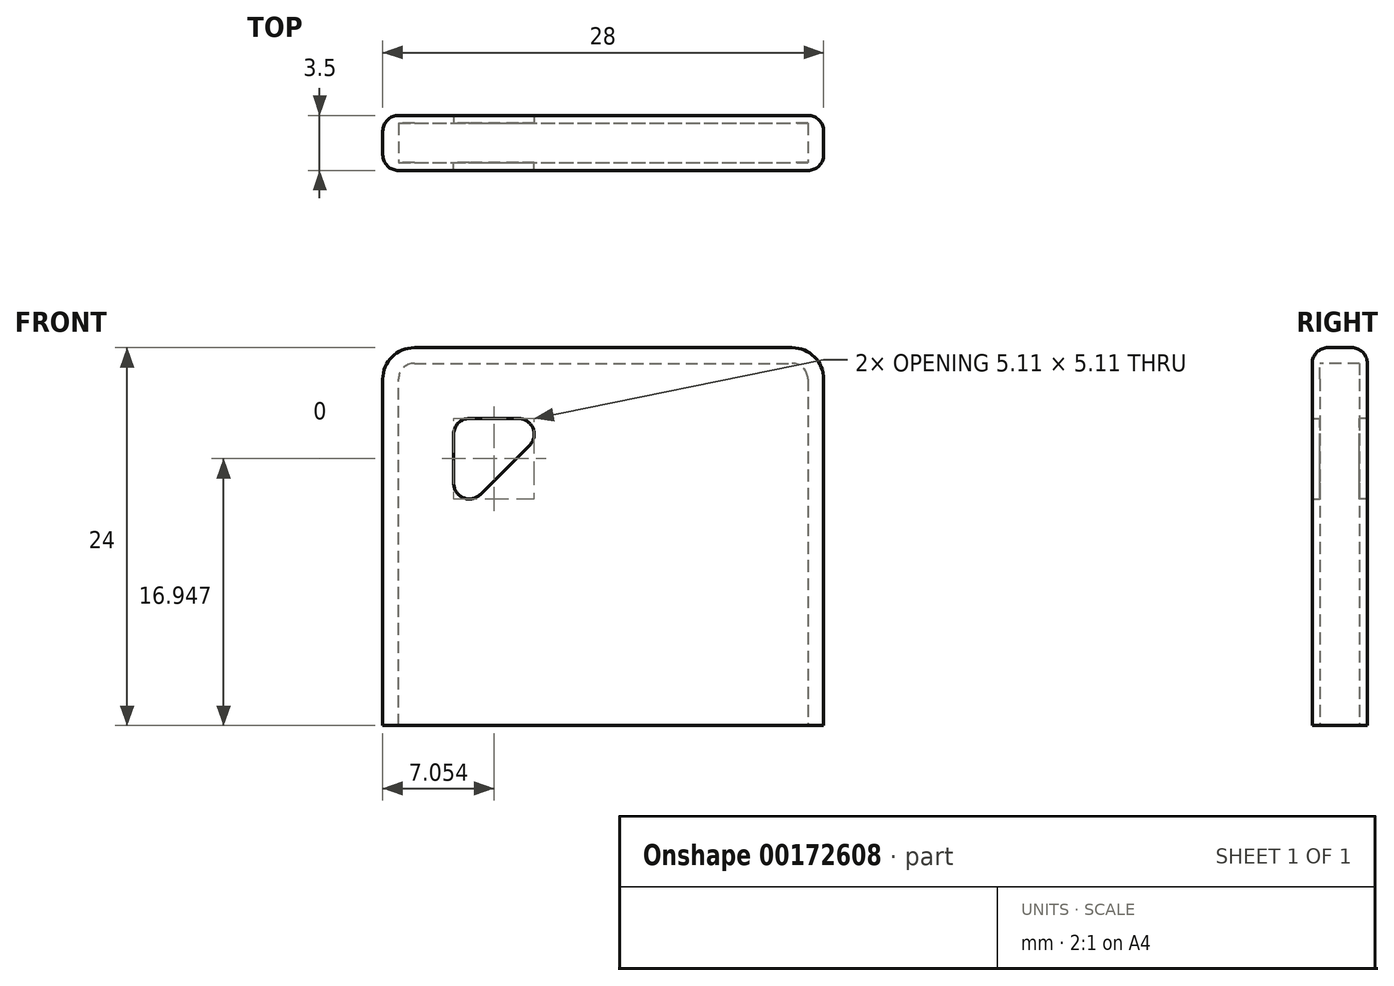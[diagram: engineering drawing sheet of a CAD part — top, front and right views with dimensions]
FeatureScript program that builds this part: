
annotation { "Feature Type Name" : "Feature", "Feature Type Description" : "" }
export const myFeature = defineFeature(function(context is Context, id is Id, definition is map)
    precondition{}
    {
        {
            var Q0;
            Q0=qCreatedBy(makeId("Front.planeOp"),FACE);
            var sketch = newSketch(context, id + "F0", { "sketchPlane" : qUnion([Q0])});
            skLineSegment(sketch, "E0", {"start": v(-50.86, -19) * mm, "end": v(-22.86, -19) * mm});
            skLineSegment(sketch, "E1", {"start": v(-22.86, -19) * mm, "end": v(-22.86, 0) * mm});
            skLineSegment(sketch, "E2", {"start": v(-50.86, -19) * mm, "end": v(-50.86, 0) * mm});
            skLineSegment(sketch, "E3", {"start": v(-45.86, 5) * mm, "end": v(-27.86, 5) * mm});
            skLineSegment(sketch, "E4", {"start": v(-50.86, -19) * mm, "end": v(-50.86, 3) * mm});
            skLineSegment(sketch, "E5", {"start": v(-48.86, 5) * mm, "end": v(-24.86, 5) * mm});
            skLineSegment(sketch, "E6", {"start": v(-22.86, -19) * mm, "end": v(-22.86, 3) * mm});
            skArc(sketch, "E7.filletArc", {"start": v(-22.86, 3) * mm, "mid": v(-23.45, 4.41) * mm, "end": v(-24.86, 5) * mm});
            skArc(sketch, "E8.filletArc", {"start": v(-48.86, 5) * mm, "mid": v(-50.27, 4.41) * mm, "end": v(-50.86, 3) * mm});
            skLineSegment(sketch, "E9", {"start": v(-44.65, -4.32) * mm, "end": v(-41.54, -1.2) * mm});
            skLineSegment(sketch, "E10", {"start": v(-46.36, -3.61) * mm, "end": v(-46.36, -0.5) * mm});
            skLineSegment(sketch, "E11", {"start": v(-42.25, 0.5) * mm, "end": v(-45.36, 0.5) * mm});
            skArc(sketch, "E12.filletArc", {"start": v(-45.36, 0.5) * mm, "mid": v(-46.07, 0.2) * mm, "end": v(-46.36, -0.5) * mm});
            skArc(sketch, "E13.filletArc", {"start": v(-41.54, -1.2) * mm, "mid": v(-41.32, -0.12) * mm, "end": v(-42.25, 0.5) * mm});
            skArc(sketch, "E14.filletArc", {"start": v(-46.36, -3.61) * mm, "mid": v(-45.74, -4.54) * mm, "end": v(-44.65, -4.32) * mm});
            skLineSegment(sketch, "E15", {"start": v(-49.86, -19) * mm, "end": v(-49.86, 3) * mm});
            skLineSegment(sketch, "E16", {"start": v(-48.86, 4) * mm, "end": v(-24.86, 4) * mm});
            skLineSegment(sketch, "E17", {"start": v(-23.86, 3) * mm, "end": v(-23.86, -19) * mm});
            skPoint(sketch, "E18.visualSharp", {"position": v(-49.86, 4) * mm});
            skArc(sketch, "E18.filletArc", {"start": v(-48.86, 4) * mm, "mid": v(-49.57, 3.7) * mm, "end": v(-49.86, 3) * mm});
            skPoint(sketch, "E19.visualSharp", {"position": v(-23.86, 4) * mm});
            skArc(sketch, "E19.filletArc", {"start": v(-23.86, 3) * mm, "mid": v(-24.15, 3.7) * mm, "end": v(-24.86, 4) * mm});
            skSolve(sketch);
        }
        {
            var Q0;
            {var subQ5=sQuery(id+"F0.wireOp",EDGE,"E7.filletArc");Q0=makeQuery(id+"F0.imprint","IMPRINT",FACE,{"disambiguationData":[TD([[makeQuery(id+"F0.imprint","IMPRINT",EDGE,{"derivedFrom":subQ5}),1.0]])]});}
            var Q1;
            Q1=makeQuery(id+"F0.imprint","IMPRINT",FACE,{"disambiguationData":[TD([[makeQuery(id+"F0.imprint","IMPRINT",EDGE,{"derivedFrom":sQuery(id+"F0.wireOp",EDGE,"E9")}),-1.0]])]});
            extrude(context, id + "F1", {"entities" : qUnion([Q0, Q1]), "depth" : 0.5 * mm});
        }
        {
            var Q0;
            {var subQ5=sQuery(id+"F0.wireOp",EDGE,"E7.filletArc");Q0=makeQuery(id+"F0.imprint","IMPRINT",FACE,{"disambiguationData":[TD([[makeQuery(id+"F0.imprint","IMPRINT",EDGE,{"derivedFrom":subQ5}),1.0]])]});}
            extrude(context, id + "F2", {"entities" : qUnion([Q0]), "operationType" : NewBodyOperationType.ADD, "oppositeDirection" : true, "depth" : 1.25 * mm});
        }
        {
            var Q0;
            Q0=makeQuery(id+"F2.opExtrude","CAP_FACE",FACE,{"disambiguationData":[OSD([sQuery(id+"F0.wireOp",EDGE,"E0"),sQuery(id+"F0.wireOp",EDGE,"E4"),sQuery(id+"F0.wireOp",EDGE,"E5"),sQuery(id+"F0.wireOp",EDGE,"E6"),sQuery(id+"F0.wireOp",EDGE,"E7.filletArc"),sQuery(id+"F0.wireOp",EDGE,"E8.filletArc"),sQuery(id+"F0.wireOp",EDGE,"E15"),sQuery(id+"F0.wireOp",EDGE,"E16"),sQuery(id+"F0.wireOp",EDGE,"E17"),sQuery(id+"F0.wireOp",EDGE,"E18.filletArc"),sQuery(id+"F0.wireOp",EDGE,"E19.filletArc")])],"isStart":false});
            cPlane(context, id + "F3", {"entities" : qUnion([Q0]), "cplaneType" : CPlaneType.OFFSET, "offset" : 0 * mm, "width" : 150 * mm, "height" : 150 * mm});
        }
        {
            var Q0;
            Q0=makeQuery(id+"F1.opExtrude","SWEPT_BODY",BODY,{"disambiguationData":[OSD([sQuery(id+"F0.wireOp",EDGE,"E0"),sQuery(id+"F0.wireOp",EDGE,"E4"),sQuery(id+"F0.wireOp",EDGE,"E5"),sQuery(id+"F0.wireOp",EDGE,"E6"),sQuery(id+"F0.wireOp",EDGE,"E7.filletArc"),sQuery(id+"F0.wireOp",EDGE,"E8.filletArc"),sQuery(id+"F0.wireOp",EDGE,"E9"),sQuery(id+"F0.wireOp",EDGE,"E10"),sQuery(id+"F0.wireOp",EDGE,"E11"),sQuery(id+"F0.wireOp",EDGE,"E12.filletArc"),sQuery(id+"F0.wireOp",EDGE,"E13.filletArc"),sQuery(id+"F0.wireOp",EDGE,"E14.filletArc")])]});
            var Q1;
            Q1=qCreatedBy(id+"F3.planeOp",FACE);
            mirror(context, id + "F4", {"operationType" : NewBodyOperationType.ADD, "entities" : qUnion([Q0]), "mirrorPlane" : qUnion([Q1])});
        }
        {
            var Q0;
            Q0=makeQuery(id+"F4.opPattern","COPY",EDGE,{"derivedFrom":makeQuery(id+"F1.opExtrude","CAP_EDGE",EDGE,{"disambiguationData":[OSD([sQuery(id+"F0.wireOp",EDGE,"E4")])],"isStart":false}),"instanceName":"1"});
            var Q1;
            Q1=makeQuery(id+"F1.opExtrude","CAP_EDGE",EDGE,{"disambiguationData":[OSD([sQuery(id+"F0.wireOp",EDGE,"E4")])],"isStart":false});
            fillet(context, id + "F5", {"entities" : qUnion([Q0, Q1]), "radius" : 1 * mm, "tangentPropagation" : true, "allowEdgeOverflow" : false});
        }
    });
